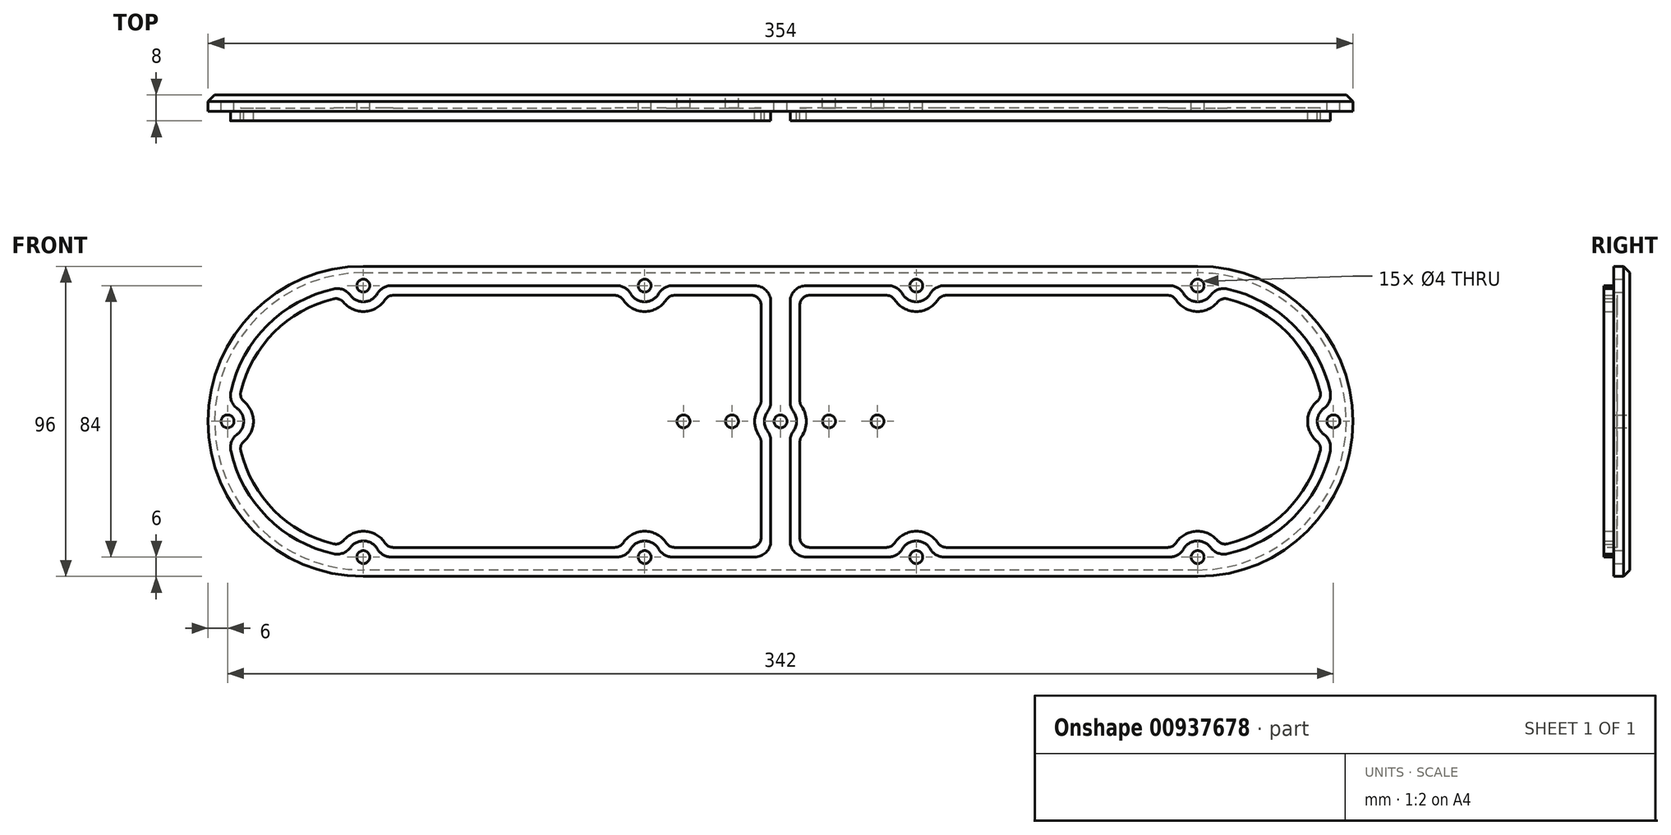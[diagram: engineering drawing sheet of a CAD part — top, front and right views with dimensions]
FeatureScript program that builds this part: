
annotation { "Feature Type Name" : "Feature", "Feature Type Description" : "" }
export const myFeature = defineFeature(function(context is Context, id is Id, definition is map)
    precondition{}
    {
        {
            var Q0;
            Q0=qCreatedBy(makeId("Front.planeOp"),FACE);
            var sketch = newSketch(context, id + "F0", { "sketchPlane" : qUnion([Q0])});
            skLineSegment(sketch, "E0", {"start": v(0, -113.77) * mm, "end": v(0, 113.17) * mm, "construction": true});
            skArc(sketch, "E1", {"start": v(129, 48) * mm, "mid": v(177, 0) * mm, "end": v(129, -48) * mm});
            skLineSegment(sketch, "E2", {"start": v(129, -48) * mm, "end": v(0, -48) * mm});
            skLineSegment(sketch, "E3", {"start": v(129, 48) * mm, "end": v(0, 48) * mm});
            skLineSegment(sketch, "E4.MirrorCS", {"start": v(-129, -48) * mm, "end": v(0, -48) * mm});
            skLineSegment(sketch, "E5.MirrorCS", {"start": v(-129, 48) * mm, "end": v(0, 48) * mm});
            skArc(sketch, "E6.MirrorCS", {"start": v(-129, 48) * mm, "mid": v(-177, 0) * mm, "end": v(-129, -48) * mm});
            skLineSegment(sketch, "E7", {"start": v(124, 42) * mm, "end": v(47, 42) * mm});
            skLineSegment(sketch, "E8", {"start": v(124, -42) * mm, "end": v(47, -42) * mm});
            skLineSegment(sketch, "E9", {"start": v(3, 42) * mm, "end": v(3, 4) * mm});
            skLineSegment(sketch, "E10.MirrorCS", {"start": v(-3, 42) * mm, "end": v(-3, 4) * mm});
            skCircle(sketch, "E11", {"center": v(42, 42) * mm, "radius": 2 * mm});
            skCircle(sketch, "E12.1.0", {"center": v(42, -42) * mm, "radius": 2 * mm});
            skCircle(sketch, "E13", {"center": v(0, 0) * mm, "radius": 2 * mm});
            skArc(sketch, "E14", {"start": v(170.7, 5) * mm, "mid": v(166, 0) * mm, "end": v(170.7, -5) * mm});
            skArc(sketch, "E15.trimOffspring", {"start": v(170.7, 5) * mm, "mid": v(158.7, 29.7) * mm, "end": v(134, 41.7) * mm});
            skArc(sketch, "E16", {"start": v(124, 42) * mm, "mid": v(128.85, 37) * mm, "end": v(134, 41.7) * mm});
            skArc(sketch, "E17", {"start": v(-3, 4) * mm, "mid": v(-5, 0) * mm, "end": v(-3, -4) * mm});
            skLineSegment(sketch, "E18.trimOffspring", {"start": v(-3, -4) * mm, "end": v(-3, -42) * mm});
            skLineSegment(sketch, "E19.trimOffspring", {"start": v(3, -4) * mm, "end": v(3, -42) * mm});
            skArc(sketch, "E20.trimOffspring", {"start": v(3, -4) * mm, "mid": v(5, 0) * mm, "end": v(3, 4) * mm});
            skArc(sketch, "E21", {"start": v(124, -42) * mm, "mid": v(128.85, -37) * mm, "end": v(134, -41.7) * mm});
            skArc(sketch, "E22.trimOffspring", {"start": v(134, -41.7) * mm, "mid": v(158.7, -29.7) * mm, "end": v(170.7, -5) * mm});
            skArc(sketch, "E23", {"start": v(37, 42) * mm, "mid": v(42, 37) * mm, "end": v(47, 42) * mm});
            skLineSegment(sketch, "E24.trimOffspring", {"start": v(37, 42) * mm, "end": v(3, 42) * mm});
            skArc(sketch, "E25", {"start": v(37, -42) * mm, "mid": v(42, -37) * mm, "end": v(47, -42) * mm});
            skLineSegment(sketch, "E26.trimOffspring", {"start": v(37, -42) * mm, "end": v(3, -42) * mm});
            skLineSegment(sketch, "E27.MirrorCS", {"start": v(-37, 42) * mm, "end": v(-3, 42) * mm});
            skLineSegment(sketch, "E28.MirrorCS", {"start": v(-124, 42) * mm, "end": v(-47, 42) * mm});
            skArc(sketch, "E29.MirrorCS", {"start": v(-37, 42) * mm, "mid": v(-42, 37) * mm, "end": v(-47, 42) * mm});
            skArc(sketch, "E30.MirrorCS", {"start": v(-124, 42) * mm, "mid": v(-128.85, 37) * mm, "end": v(-134, 41.7) * mm});
            skArc(sketch, "E31.MirrorCS", {"start": v(-170.7, 5) * mm, "mid": v(-158.7, 29.7) * mm, "end": v(-134, 41.7) * mm});
            skArc(sketch, "E32.MirrorCS", {"start": v(-170.7, 5) * mm, "mid": v(-166, 0) * mm, "end": v(-170.7, -5) * mm});
            skArc(sketch, "E33.MirrorCS", {"start": v(-134, -41.7) * mm, "mid": v(-158.7, -29.7) * mm, "end": v(-170.7, -5) * mm});
            skLineSegment(sketch, "E34.MirrorCS", {"start": v(-37, -42) * mm, "end": v(-3, -42) * mm});
            skArc(sketch, "E35.MirrorCS", {"start": v(-37, -42) * mm, "mid": v(-42, -37) * mm, "end": v(-47, -42) * mm});
            skLineSegment(sketch, "E36.MirrorCS", {"start": v(-124, -42) * mm, "end": v(-47, -42) * mm});
            skArc(sketch, "E37.MirrorCS", {"start": v(-124, -42) * mm, "mid": v(-128.85, -37) * mm, "end": v(-134, -41.7) * mm});
            skLineSegment(sketch, "E38", {"start": v(-28.33, 0) * mm, "end": v(22.4, 0) * mm, "construction": true});
            skCircle(sketch, "E39", {"center": v(129, 42) * mm, "radius": 2 * mm});
            skCircle(sketch, "E40.2.0", {"center": v(129, -42) * mm, "radius": 2 * mm});
            skCircle(sketch, "E40.3.0", {"center": v(171, 0) * mm, "radius": 2 * mm});
            skCircle(sketch, "E41.MirrorC", {"center": v(-42, 42) * mm, "radius": 2 * mm});
            skCircle(sketch, "E42.MirrorC", {"center": v(-129, 42) * mm, "radius": 2 * mm});
            skCircle(sketch, "E43.MirrorC", {"center": v(-171, 0) * mm, "radius": 2 * mm});
            skCircle(sketch, "E44.MirrorC", {"center": v(-129, -42) * mm, "radius": 2 * mm});
            skCircle(sketch, "E45.MirrorC", {"center": v(-42, -42) * mm, "radius": 2 * mm});
            skLineSegment(sketch, "E46.0", {"start": v(34.58, 39) * mm, "end": v(6, 39) * mm});
            skArc(sketch, "E46.1", {"start": v(34.58, 39) * mm, "mid": v(42, 34) * mm, "end": v(49.42, 39) * mm});
            skLineSegment(sketch, "E46.2", {"start": v(121.58, 39) * mm, "end": v(49.42, 39) * mm});
            skArc(sketch, "E46.3", {"start": v(34.58, -39) * mm, "mid": v(42, -34) * mm, "end": v(49.42, -39) * mm});
            skLineSegment(sketch, "E46.4", {"start": v(34.58, -39) * mm, "end": v(6, -39) * mm});
            skLineSegment(sketch, "E46.5", {"start": v(6, -5.3) * mm, "end": v(6, -39) * mm});
            skArc(sketch, "E46.6", {"start": v(6, -5.3) * mm, "mid": v(8, 0) * mm, "end": v(6, 5.3) * mm});
            skLineSegment(sketch, "E46.7", {"start": v(121.58, -39) * mm, "end": v(49.42, -39) * mm});
            skArc(sketch, "E46.8", {"start": v(121.58, -39) * mm, "mid": v(128.64, -34) * mm, "end": v(136.12, -38.35) * mm});
            skArc(sketch, "E46.9", {"start": v(136.12, -38.35) * mm, "mid": v(156.58, -27.58) * mm, "end": v(167.35, -7.12) * mm});
            skLineSegment(sketch, "E46.10", {"start": v(6, 39) * mm, "end": v(6, 5.3) * mm});
            skArc(sketch, "E46.11", {"start": v(167.35, 7.12) * mm, "mid": v(163, 0) * mm, "end": v(167.35, -7.12) * mm});
            skArc(sketch, "E46.12", {"start": v(167.35, 7.12) * mm, "mid": v(156.58, 27.58) * mm, "end": v(136.12, 38.35) * mm});
            skArc(sketch, "E46.13", {"start": v(121.58, 39) * mm, "mid": v(128.64, 34) * mm, "end": v(136.12, 38.35) * mm});
            skLineSegment(sketch, "E47.MirrorCS", {"start": v(-6, -5.3) * mm, "end": v(-6, -39) * mm});
            skArc(sketch, "E48.MirrorCS", {"start": v(-6, -5.3) * mm, "mid": v(-8, 0) * mm, "end": v(-6, 5.3) * mm});
            skLineSegment(sketch, "E49.MirrorCS", {"start": v(-6, 39) * mm, "end": v(-6, 5.3) * mm});
            skLineSegment(sketch, "E50.MirrorCS", {"start": v(-34.58, 39) * mm, "end": v(-6, 39) * mm});
            skLineSegment(sketch, "E51.MirrorCS", {"start": v(-121.58, 39) * mm, "end": v(-49.42, 39) * mm});
            skArc(sketch, "E52.MirrorCS", {"start": v(-34.58, 39) * mm, "mid": v(-42, 34) * mm, "end": v(-49.42, 39) * mm});
            skArc(sketch, "E53.MirrorCS", {"start": v(-121.58, 39) * mm, "mid": v(-128.64, 34) * mm, "end": v(-136.12, 38.35) * mm});
            skArc(sketch, "E54.MirrorCS", {"start": v(-167.35, 7.12) * mm, "mid": v(-156.58, 27.58) * mm, "end": v(-136.12, 38.35) * mm});
            skArc(sketch, "E55.MirrorCS", {"start": v(-167.35, 7.12) * mm, "mid": v(-163, 0) * mm, "end": v(-167.35, -7.12) * mm});
            skArc(sketch, "E56.MirrorCS", {"start": v(-136.12, -38.35) * mm, "mid": v(-156.58, -27.58) * mm, "end": v(-167.35, -7.12) * mm});
            skArc(sketch, "E57.MirrorCS", {"start": v(-121.58, -39) * mm, "mid": v(-128.64, -34) * mm, "end": v(-136.12, -38.35) * mm});
            skLineSegment(sketch, "E58.MirrorCS", {"start": v(-121.58, -39) * mm, "end": v(-49.42, -39) * mm});
            skArc(sketch, "E59.MirrorCS", {"start": v(-34.58, -39) * mm, "mid": v(-42, -34) * mm, "end": v(-49.42, -39) * mm});
            skLineSegment(sketch, "E60.MirrorCS", {"start": v(-34.58, -39) * mm, "end": v(-6, -39) * mm});
            skCircle(sketch, "E61", {"center": v(15, 0) * mm, "radius": 2 * mm});
            skCircle(sketch, "E62", {"center": v(30, 0) * mm, "radius": 2 * mm});
            skCircle(sketch, "E63.MirrorC", {"center": v(-15, 0) * mm, "radius": 2 * mm});
            skCircle(sketch, "E64.MirrorC", {"center": v(-30, 0) * mm, "radius": 2 * mm});
            skSolve(sketch);
        }
        {
            var Q0;
            Q0=qSketchRegion(id+"F0",true);
            extrude(context, id + "F1", {"entities" : qUnion([Q0]), "depth" : 5 * mm, "offsetDistance" : 25 * mm});
        }
        {
            var Q0;
            Q0=makeQuery(id+"F1.opExtrude","SWEPT_EDGE",EDGE,{"disambiguationData":[OSD([sQuery(id+"F0.wireOp",EDGE,"E9"),sQuery(id+"F0.wireOp",EDGE,"E24.trimOffspring")])]});
            var Q1;
            Q1=makeQuery(id+"F1.opExtrude","SWEPT_EDGE",EDGE,{"disambiguationData":[OSD([sQuery(id+"F0.wireOp",EDGE,"E19.trimOffspring"),sQuery(id+"F0.wireOp",EDGE,"E26.trimOffspring")])]});
            var Q2;
            Q2=makeQuery(id+"F1.opExtrude","SWEPT_EDGE",EDGE,{"disambiguationData":[OSD([sQuery(id+"F0.wireOp",EDGE,"E25"),sQuery(id+"F0.wireOp",EDGE,"E26.trimOffspring")])]});
            var Q3;
            Q3=makeQuery(id+"F1.opExtrude","SWEPT_EDGE",EDGE,{"disambiguationData":[OSD([sQuery(id+"F0.wireOp",EDGE,"E8"),sQuery(id+"F0.wireOp",EDGE,"E25")])]});
            var Q4;
            Q4=makeQuery(id+"F1.opExtrude","SWEPT_EDGE",EDGE,{"disambiguationData":[OSD([sQuery(id+"F0.wireOp",EDGE,"E8"),sQuery(id+"F0.wireOp",EDGE,"E21")])]});
            var Q5;
            Q5=makeQuery(id+"F1.opExtrude","SWEPT_EDGE",EDGE,{"disambiguationData":[OSD([sQuery(id+"F0.wireOp",EDGE,"E21"),sQuery(id+"F0.wireOp",EDGE,"E22.trimOffspring")])]});
            var Q6;
            Q6=makeQuery(id+"F1.opExtrude","SWEPT_EDGE",EDGE,{"disambiguationData":[OSD([sQuery(id+"F0.wireOp",EDGE,"E14"),sQuery(id+"F0.wireOp",EDGE,"E22.trimOffspring")])]});
            var Q7;
            Q7=makeQuery(id+"F1.opExtrude","SWEPT_EDGE",EDGE,{"disambiguationData":[OSD([sQuery(id+"F0.wireOp",EDGE,"E14"),sQuery(id+"F0.wireOp",EDGE,"E15.trimOffspring")])]});
            var Q8;
            Q8=makeQuery(id+"F1.opExtrude","SWEPT_EDGE",EDGE,{"disambiguationData":[OSD([sQuery(id+"F0.wireOp",EDGE,"E7"),sQuery(id+"F0.wireOp",EDGE,"E16")])]});
            var Q9;
            Q9=makeQuery(id+"F1.opExtrude","SWEPT_EDGE",EDGE,{"disambiguationData":[OSD([sQuery(id+"F0.wireOp",EDGE,"E15.trimOffspring"),sQuery(id+"F0.wireOp",EDGE,"E16")])]});
            var Q10;
            Q10=makeQuery(id+"F1.opExtrude","SWEPT_EDGE",EDGE,{"disambiguationData":[OSD([sQuery(id+"F0.wireOp",EDGE,"E7"),sQuery(id+"F0.wireOp",EDGE,"E23")])]});
            var Q11;
            Q11=makeQuery(id+"F1.opExtrude","SWEPT_EDGE",EDGE,{"disambiguationData":[OSD([sQuery(id+"F0.wireOp",EDGE,"E23"),sQuery(id+"F0.wireOp",EDGE,"E24.trimOffspring")])]});
            var Q12;
            Q12=makeQuery(id+"F1.opExtrude","SWEPT_EDGE",EDGE,{"disambiguationData":[OSD([sQuery(id+"F0.wireOp",EDGE,"E19.trimOffspring"),sQuery(id+"F0.wireOp",EDGE,"E20.trimOffspring")])]});
            var Q13;
            Q13=makeQuery(id+"F1.opExtrude","SWEPT_EDGE",EDGE,{"disambiguationData":[OSD([sQuery(id+"F0.wireOp",EDGE,"E9"),sQuery(id+"F0.wireOp",EDGE,"E20.trimOffspring")])]});
            var Q14;
            Q14=makeQuery(id+"F1.opExtrude","SWEPT_EDGE",EDGE,{"disambiguationData":[OSD([sQuery(id+"F0.wireOp",EDGE,"E10.MirrorCS"),sQuery(id+"F0.wireOp",EDGE,"E27.MirrorCS")])]});
            var Q15;
            Q15=makeQuery(id+"F1.opExtrude","SWEPT_EDGE",EDGE,{"disambiguationData":[OSD([sQuery(id+"F0.wireOp",EDGE,"E17"),sQuery(id+"F0.wireOp",EDGE,"E18.trimOffspring")])]});
            var Q16;
            Q16=makeQuery(id+"F1.opExtrude","SWEPT_EDGE",EDGE,{"disambiguationData":[OSD([sQuery(id+"F0.wireOp",EDGE,"E10.MirrorCS"),sQuery(id+"F0.wireOp",EDGE,"E17")])]});
            var Q17;
            Q17=makeQuery(id+"F1.opExtrude","SWEPT_EDGE",EDGE,{"disambiguationData":[OSD([sQuery(id+"F0.wireOp",EDGE,"E18.trimOffspring"),sQuery(id+"F0.wireOp",EDGE,"E34.MirrorCS")])]});
            var Q18;
            Q18=makeQuery(id+"F1.opExtrude","SWEPT_EDGE",EDGE,{"disambiguationData":[OSD([sQuery(id+"F0.wireOp",EDGE,"E35.MirrorCS"),sQuery(id+"F0.wireOp",EDGE,"E36.MirrorCS")])]});
            var Q19;
            Q19=makeQuery(id+"F1.opExtrude","SWEPT_EDGE",EDGE,{"disambiguationData":[OSD([sQuery(id+"F0.wireOp",EDGE,"E34.MirrorCS"),sQuery(id+"F0.wireOp",EDGE,"E35.MirrorCS")])]});
            var Q20;
            Q20=makeQuery(id+"F1.opExtrude","SWEPT_EDGE",EDGE,{"disambiguationData":[OSD([sQuery(id+"F0.wireOp",EDGE,"E36.MirrorCS"),sQuery(id+"F0.wireOp",EDGE,"E37.MirrorCS")])]});
            var Q21;
            Q21=makeQuery(id+"F1.opExtrude","SWEPT_EDGE",EDGE,{"disambiguationData":[OSD([sQuery(id+"F0.wireOp",EDGE,"E33.MirrorCS"),sQuery(id+"F0.wireOp",EDGE,"E37.MirrorCS")])]});
            var Q22;
            Q22=makeQuery(id+"F1.opExtrude","SWEPT_EDGE",EDGE,{"disambiguationData":[OSD([sQuery(id+"F0.wireOp",EDGE,"E31.MirrorCS"),sQuery(id+"F0.wireOp",EDGE,"E32.MirrorCS")])]});
            var Q23;
            Q23=makeQuery(id+"F1.opExtrude","SWEPT_EDGE",EDGE,{"disambiguationData":[OSD([sQuery(id+"F0.wireOp",EDGE,"E32.MirrorCS"),sQuery(id+"F0.wireOp",EDGE,"E33.MirrorCS")])]});
            var Q24;
            Q24=makeQuery(id+"F1.opExtrude","SWEPT_EDGE",EDGE,{"disambiguationData":[OSD([sQuery(id+"F0.wireOp",EDGE,"E28.MirrorCS"),sQuery(id+"F0.wireOp",EDGE,"E30.MirrorCS")])]});
            var Q25;
            Q25=makeQuery(id+"F1.opExtrude","SWEPT_EDGE",EDGE,{"disambiguationData":[OSD([sQuery(id+"F0.wireOp",EDGE,"E30.MirrorCS"),sQuery(id+"F0.wireOp",EDGE,"E31.MirrorCS")])]});
            var Q26;
            Q26=makeQuery(id+"F1.opExtrude","SWEPT_EDGE",EDGE,{"disambiguationData":[OSD([sQuery(id+"F0.wireOp",EDGE,"E28.MirrorCS"),sQuery(id+"F0.wireOp",EDGE,"E29.MirrorCS")])]});
            var Q27;
            Q27=makeQuery(id+"F1.opExtrude","SWEPT_EDGE",EDGE,{"disambiguationData":[OSD([sQuery(id+"F0.wireOp",EDGE,"E27.MirrorCS"),sQuery(id+"F0.wireOp",EDGE,"E29.MirrorCS")])]});
            fillet(context, id + "F2", {"entities" : qUnion([Q0, Q1, Q2, Q3, Q4, Q5, Q6, Q7, Q8, Q9, Q10, Q11, Q12, Q13, Q14, Q15, Q16, Q17, Q18, Q19, Q20, Q21, Q22, Q23, Q24, Q25, Q26, Q27]), "radius" : 5 * mm, "tangentPropagation" : true, "allowEdgeOverflow" : false});
        }
        {
            var Q0;
            Q0=makeQuery(id+"F0.imprint","IMPRINT",FACE,{"disambiguationData":[TD([[makeQuery(id+"F0.imprint","IMPRINT",EDGE,{"derivedFrom":sQuery(id+"F0.wireOp",EDGE,"E10.MirrorCS")}),-1.0]])]});
            var Q1;
            Q1=makeQuery(id+"F0.imprint","IMPRINT",FACE,{"disambiguationData":[TD([[makeQuery(id+"F0.imprint","IMPRINT",EDGE,{"derivedFrom":sQuery(id+"F0.wireOp",EDGE,"E7")}),1.0]])]});
            extrude(context, id + "F3", {"entities" : qUnion([Q0, Q1]), "operationType" : NewBodyOperationType.ADD, "depth" : 8 * mm, "offsetDistance" : 25 * mm});
        }
        {
            var Q0;
            Q0=makeQuery(id+"F0.imprint","IMPRINT",FACE,{"disambiguationData":[TD([[makeQuery(id+"F0.imprint","IMPRINT",EDGE,{"derivedFrom":sQuery(id+"F0.wireOp",EDGE,"E46.0")}),1.0]])]});
            var Q1;
            Q1=makeQuery(id+"F0.imprint","IMPRINT",FACE,{"disambiguationData":[TD([[makeQuery(id+"F0.imprint","IMPRINT",EDGE,{"derivedFrom":sQuery(id+"F0.wireOp",EDGE,"E47.MirrorCS")}),-1.0]])]});
            extrude(context, id + "F4", {"entities" : qUnion([Q0, Q1]), "operationType" : NewBodyOperationType.ADD, "depth" : 4 * mm, "offsetDistance" : 25 * mm});
        }
        {
            var Q0;
            Q0=makeQuery(id+"F3.opExtrude","SWEPT_EDGE",EDGE,{"disambiguationData":[OSD([sQuery(id+"F0.wireOp",EDGE,"E23"),sQuery(id+"F0.wireOp",EDGE,"E24.trimOffspring")])]});
            var Q1;
            Q1=makeQuery(id+"F3.opExtrude","SWEPT_EDGE",EDGE,{"disambiguationData":[OSD([sQuery(id+"F0.wireOp",EDGE,"E7"),sQuery(id+"F0.wireOp",EDGE,"E23")])]});
            var Q2;
            Q2=makeQuery(id+"F3.opExtrude","SWEPT_EDGE",EDGE,{"disambiguationData":[OSD([sQuery(id+"F0.wireOp",EDGE,"E7"),sQuery(id+"F0.wireOp",EDGE,"E16")])]});
            var Q3;
            Q3=makeQuery(id+"F3.opExtrude","SWEPT_EDGE",EDGE,{"disambiguationData":[OSD([sQuery(id+"F0.wireOp",EDGE,"E15.trimOffspring"),sQuery(id+"F0.wireOp",EDGE,"E16")])]});
            var Q4;
            Q4=makeQuery(id+"F3.opExtrude","SWEPT_EDGE",EDGE,{"disambiguationData":[OSD([sQuery(id+"F0.wireOp",EDGE,"E14"),sQuery(id+"F0.wireOp",EDGE,"E15.trimOffspring")])]});
            var Q5;
            Q5=makeQuery(id+"F3.opExtrude","SWEPT_EDGE",EDGE,{"disambiguationData":[OSD([sQuery(id+"F0.wireOp",EDGE,"E14"),sQuery(id+"F0.wireOp",EDGE,"E22.trimOffspring")])]});
            var Q6;
            Q6=makeQuery(id+"F3.opExtrude","SWEPT_EDGE",EDGE,{"disambiguationData":[OSD([sQuery(id+"F0.wireOp",EDGE,"E21"),sQuery(id+"F0.wireOp",EDGE,"E22.trimOffspring")])]});
            var Q7;
            Q7=makeQuery(id+"F3.opExtrude","SWEPT_EDGE",EDGE,{"disambiguationData":[OSD([sQuery(id+"F0.wireOp",EDGE,"E8"),sQuery(id+"F0.wireOp",EDGE,"E21")])]});
            var Q8;
            Q8=makeQuery(id+"F3.opExtrude","SWEPT_EDGE",EDGE,{"disambiguationData":[OSD([sQuery(id+"F0.wireOp",EDGE,"E8"),sQuery(id+"F0.wireOp",EDGE,"E25")])]});
            var Q9;
            Q9=makeQuery(id+"F3.opExtrude","SWEPT_EDGE",EDGE,{"disambiguationData":[OSD([sQuery(id+"F0.wireOp",EDGE,"E25"),sQuery(id+"F0.wireOp",EDGE,"E26.trimOffspring")])]});
            var Q10;
            Q10=makeQuery(id+"F3.opExtrude","SWEPT_EDGE",EDGE,{"disambiguationData":[OSD([sQuery(id+"F0.wireOp",EDGE,"E19.trimOffspring"),sQuery(id+"F0.wireOp",EDGE,"E26.trimOffspring")])]});
            var Q11;
            Q11=makeQuery(id+"F3.opExtrude","SWEPT_EDGE",EDGE,{"disambiguationData":[OSD([sQuery(id+"F0.wireOp",EDGE,"E19.trimOffspring"),sQuery(id+"F0.wireOp",EDGE,"E20.trimOffspring")])]});
            var Q12;
            Q12=makeQuery(id+"F3.opExtrude","SWEPT_EDGE",EDGE,{"disambiguationData":[OSD([sQuery(id+"F0.wireOp",EDGE,"E9"),sQuery(id+"F0.wireOp",EDGE,"E20.trimOffspring")])]});
            var Q13;
            Q13=makeQuery(id+"F3.opExtrude","SWEPT_EDGE",EDGE,{"disambiguationData":[OSD([sQuery(id+"F0.wireOp",EDGE,"E10.MirrorCS"),sQuery(id+"F0.wireOp",EDGE,"E17")])]});
            var Q14;
            Q14=makeQuery(id+"F3.opExtrude","SWEPT_EDGE",EDGE,{"disambiguationData":[OSD([sQuery(id+"F0.wireOp",EDGE,"E17"),sQuery(id+"F0.wireOp",EDGE,"E18.trimOffspring")])]});
            var Q15;
            Q15=makeQuery(id+"F3.opExtrude","SWEPT_EDGE",EDGE,{"disambiguationData":[OSD([sQuery(id+"F0.wireOp",EDGE,"E10.MirrorCS"),sQuery(id+"F0.wireOp",EDGE,"E27.MirrorCS")])]});
            var Q16;
            Q16=makeQuery(id+"F3.opExtrude","SWEPT_EDGE",EDGE,{"disambiguationData":[OSD([sQuery(id+"F0.wireOp",EDGE,"E9"),sQuery(id+"F0.wireOp",EDGE,"E24.trimOffspring")])]});
            var Q17;
            Q17=makeQuery(id+"F3.opExtrude","SWEPT_EDGE",EDGE,{"disambiguationData":[OSD([sQuery(id+"F0.wireOp",EDGE,"E27.MirrorCS"),sQuery(id+"F0.wireOp",EDGE,"E29.MirrorCS")])]});
            var Q18;
            Q18=makeQuery(id+"F3.opExtrude","SWEPT_EDGE",EDGE,{"disambiguationData":[OSD([sQuery(id+"F0.wireOp",EDGE,"E28.MirrorCS"),sQuery(id+"F0.wireOp",EDGE,"E29.MirrorCS")])]});
            var Q19;
            Q19=makeQuery(id+"F3.opExtrude","SWEPT_EDGE",EDGE,{"disambiguationData":[OSD([sQuery(id+"F0.wireOp",EDGE,"E28.MirrorCS"),sQuery(id+"F0.wireOp",EDGE,"E30.MirrorCS")])]});
            var Q20;
            Q20=makeQuery(id+"F3.opExtrude","SWEPT_EDGE",EDGE,{"disambiguationData":[OSD([sQuery(id+"F0.wireOp",EDGE,"E30.MirrorCS"),sQuery(id+"F0.wireOp",EDGE,"E31.MirrorCS")])]});
            var Q21;
            Q21=makeQuery(id+"F3.opExtrude","SWEPT_EDGE",EDGE,{"disambiguationData":[OSD([sQuery(id+"F0.wireOp",EDGE,"E31.MirrorCS"),sQuery(id+"F0.wireOp",EDGE,"E32.MirrorCS")])]});
            var Q22;
            Q22=makeQuery(id+"F3.opExtrude","SWEPT_EDGE",EDGE,{"disambiguationData":[OSD([sQuery(id+"F0.wireOp",EDGE,"E32.MirrorCS"),sQuery(id+"F0.wireOp",EDGE,"E33.MirrorCS")])]});
            var Q23;
            Q23=makeQuery(id+"F3.opExtrude","SWEPT_EDGE",EDGE,{"disambiguationData":[OSD([sQuery(id+"F0.wireOp",EDGE,"E36.MirrorCS"),sQuery(id+"F0.wireOp",EDGE,"E37.MirrorCS")])]});
            var Q24;
            Q24=makeQuery(id+"F3.opExtrude","SWEPT_EDGE",EDGE,{"disambiguationData":[OSD([sQuery(id+"F0.wireOp",EDGE,"E33.MirrorCS"),sQuery(id+"F0.wireOp",EDGE,"E37.MirrorCS")])]});
            var Q25;
            Q25=makeQuery(id+"F3.opExtrude","SWEPT_EDGE",EDGE,{"disambiguationData":[OSD([sQuery(id+"F0.wireOp",EDGE,"E35.MirrorCS"),sQuery(id+"F0.wireOp",EDGE,"E36.MirrorCS")])]});
            var Q26;
            Q26=makeQuery(id+"F3.opExtrude","SWEPT_EDGE",EDGE,{"disambiguationData":[OSD([sQuery(id+"F0.wireOp",EDGE,"E34.MirrorCS"),sQuery(id+"F0.wireOp",EDGE,"E35.MirrorCS")])]});
            var Q27;
            Q27=makeQuery(id+"F3.opExtrude","SWEPT_EDGE",EDGE,{"disambiguationData":[OSD([sQuery(id+"F0.wireOp",EDGE,"E18.trimOffspring"),sQuery(id+"F0.wireOp",EDGE,"E34.MirrorCS")])]});
            fillet(context, id + "F5", {"entities" : qUnion([Q0, Q1, Q2, Q3, Q4, Q5, Q6, Q7, Q8, Q9, Q10, Q11, Q12, Q13, Q14, Q15, Q16, Q17, Q18, Q19, Q20, Q21, Q22, Q23, Q24, Q25, Q26, Q27]), "radius" : 5 * mm, "tangentPropagation" : true, "allowEdgeOverflow" : false});
        }
        {
            var Q0;
            Q0=makeQuery(id+"F3.opExtrude","SWEPT_EDGE",EDGE,{"disambiguationData":[OSD([sQuery(id+"F0.wireOp",EDGE,"E46.6"),sQuery(id+"F0.wireOp",EDGE,"E46.10")])]});
            var Q1;
            Q1=makeQuery(id+"F3.opExtrude","SWEPT_EDGE",EDGE,{"disambiguationData":[OSD([sQuery(id+"F0.wireOp",EDGE,"E46.5"),sQuery(id+"F0.wireOp",EDGE,"E46.6")])]});
            var Q2;
            Q2=makeQuery(id+"F3.opExtrude","SWEPT_EDGE",EDGE,{"disambiguationData":[OSD([sQuery(id+"F0.wireOp",EDGE,"E47.MirrorCS"),sQuery(id+"F0.wireOp",EDGE,"E48.MirrorCS")])]});
            var Q3;
            Q3=makeQuery(id+"F3.opExtrude","SWEPT_EDGE",EDGE,{"disambiguationData":[OSD([sQuery(id+"F0.wireOp",EDGE,"E48.MirrorCS"),sQuery(id+"F0.wireOp",EDGE,"E49.MirrorCS")])]});
            var Q4;
            Q4=makeQuery(id+"F3.opExtrude","SWEPT_EDGE",EDGE,{"disambiguationData":[OSD([sQuery(id+"F0.wireOp",EDGE,"E49.MirrorCS"),sQuery(id+"F0.wireOp",EDGE,"E50.MirrorCS")])]});
            var Q5;
            Q5=makeQuery(id+"F3.opExtrude","SWEPT_EDGE",EDGE,{"disambiguationData":[OSD([sQuery(id+"F0.wireOp",EDGE,"E46.0"),sQuery(id+"F0.wireOp",EDGE,"E46.10")])]});
            var Q6;
            Q6=makeQuery(id+"F3.opExtrude","SWEPT_EDGE",EDGE,{"disambiguationData":[OSD([sQuery(id+"F0.wireOp",EDGE,"E50.MirrorCS"),sQuery(id+"F0.wireOp",EDGE,"E52.MirrorCS")])]});
            var Q7;
            Q7=makeQuery(id+"F3.opExtrude","SWEPT_EDGE",EDGE,{"disambiguationData":[OSD([sQuery(id+"F0.wireOp",EDGE,"E46.0"),sQuery(id+"F0.wireOp",EDGE,"E46.1")])]});
            var Q8;
            Q8=makeQuery(id+"F3.opExtrude","SWEPT_EDGE",EDGE,{"disambiguationData":[OSD([sQuery(id+"F0.wireOp",EDGE,"E51.MirrorCS"),sQuery(id+"F0.wireOp",EDGE,"E52.MirrorCS")])]});
            var Q9;
            Q9=makeQuery(id+"F3.opExtrude","SWEPT_EDGE",EDGE,{"disambiguationData":[OSD([sQuery(id+"F0.wireOp",EDGE,"E53.MirrorCS"),sQuery(id+"F0.wireOp",EDGE,"E54.MirrorCS")])]});
            var Q10;
            Q10=makeQuery(id+"F3.opExtrude","SWEPT_EDGE",EDGE,{"disambiguationData":[OSD([sQuery(id+"F0.wireOp",EDGE,"E51.MirrorCS"),sQuery(id+"F0.wireOp",EDGE,"E53.MirrorCS")])]});
            var Q11;
            Q11=makeQuery(id+"F3.opExtrude","SWEPT_EDGE",EDGE,{"disambiguationData":[OSD([sQuery(id+"F0.wireOp",EDGE,"E55.MirrorCS"),sQuery(id+"F0.wireOp",EDGE,"E56.MirrorCS")])]});
            var Q12;
            Q12=makeQuery(id+"F3.opExtrude","SWEPT_EDGE",EDGE,{"disambiguationData":[OSD([sQuery(id+"F0.wireOp",EDGE,"E54.MirrorCS"),sQuery(id+"F0.wireOp",EDGE,"E55.MirrorCS")])]});
            var Q13;
            Q13=makeQuery(id+"F3.opExtrude","SWEPT_EDGE",EDGE,{"disambiguationData":[OSD([sQuery(id+"F0.wireOp",EDGE,"E57.MirrorCS"),sQuery(id+"F0.wireOp",EDGE,"E58.MirrorCS")])]});
            var Q14;
            Q14=makeQuery(id+"F3.opExtrude","SWEPT_EDGE",EDGE,{"disambiguationData":[OSD([sQuery(id+"F0.wireOp",EDGE,"E56.MirrorCS"),sQuery(id+"F0.wireOp",EDGE,"E57.MirrorCS")])]});
            var Q15;
            Q15=makeQuery(id+"F3.opExtrude","SWEPT_EDGE",EDGE,{"disambiguationData":[OSD([sQuery(id+"F0.wireOp",EDGE,"E47.MirrorCS"),sQuery(id+"F0.wireOp",EDGE,"E60.MirrorCS")])]});
            var Q16;
            Q16=makeQuery(id+"F3.opExtrude","SWEPT_EDGE",EDGE,{"disambiguationData":[OSD([sQuery(id+"F0.wireOp",EDGE,"E58.MirrorCS"),sQuery(id+"F0.wireOp",EDGE,"E59.MirrorCS")])]});
            var Q17;
            Q17=makeQuery(id+"F3.opExtrude","SWEPT_EDGE",EDGE,{"disambiguationData":[OSD([sQuery(id+"F0.wireOp",EDGE,"E59.MirrorCS"),sQuery(id+"F0.wireOp",EDGE,"E60.MirrorCS")])]});
            var Q18;
            Q18=makeQuery(id+"F3.opExtrude","SWEPT_EDGE",EDGE,{"disambiguationData":[OSD([sQuery(id+"F0.wireOp",EDGE,"E46.4"),sQuery(id+"F0.wireOp",EDGE,"E46.5")])]});
            var Q19;
            Q19=makeQuery(id+"F3.opExtrude","SWEPT_EDGE",EDGE,{"disambiguationData":[OSD([sQuery(id+"F0.wireOp",EDGE,"E46.3"),sQuery(id+"F0.wireOp",EDGE,"E46.7")])]});
            var Q20;
            Q20=makeQuery(id+"F3.opExtrude","SWEPT_EDGE",EDGE,{"disambiguationData":[OSD([sQuery(id+"F0.wireOp",EDGE,"E46.3"),sQuery(id+"F0.wireOp",EDGE,"E46.4")])]});
            var Q21;
            Q21=makeQuery(id+"F3.opExtrude","SWEPT_EDGE",EDGE,{"disambiguationData":[OSD([sQuery(id+"F0.wireOp",EDGE,"E46.7"),sQuery(id+"F0.wireOp",EDGE,"E46.8")])]});
            var Q22;
            Q22=makeQuery(id+"F3.opExtrude","SWEPT_EDGE",EDGE,{"disambiguationData":[OSD([sQuery(id+"F0.wireOp",EDGE,"E46.8"),sQuery(id+"F0.wireOp",EDGE,"E46.9")])]});
            var Q23;
            Q23=makeQuery(id+"F3.opExtrude","SWEPT_EDGE",EDGE,{"disambiguationData":[OSD([sQuery(id+"F0.wireOp",EDGE,"E46.9"),sQuery(id+"F0.wireOp",EDGE,"E46.11")])]});
            var Q24;
            Q24=makeQuery(id+"F3.opExtrude","SWEPT_EDGE",EDGE,{"disambiguationData":[OSD([sQuery(id+"F0.wireOp",EDGE,"E46.11"),sQuery(id+"F0.wireOp",EDGE,"E46.12")])]});
            var Q25;
            Q25=makeQuery(id+"F3.opExtrude","SWEPT_EDGE",EDGE,{"disambiguationData":[OSD([sQuery(id+"F0.wireOp",EDGE,"E46.2"),sQuery(id+"F0.wireOp",EDGE,"E46.13")])]});
            var Q26;
            Q26=makeQuery(id+"F3.opExtrude","SWEPT_EDGE",EDGE,{"disambiguationData":[OSD([sQuery(id+"F0.wireOp",EDGE,"E46.12"),sQuery(id+"F0.wireOp",EDGE,"E46.13")])]});
            var Q27;
            Q27=makeQuery(id+"F3.opExtrude","SWEPT_EDGE",EDGE,{"disambiguationData":[OSD([sQuery(id+"F0.wireOp",EDGE,"E46.1"),sQuery(id+"F0.wireOp",EDGE,"E46.2")])]});
            fillet(context, id + "F6", {"entities" : qUnion([Q0, Q1, Q2, Q3, Q4, Q5, Q6, Q7, Q8, Q9, Q10, Q11, Q12, Q13, Q14, Q15, Q16, Q17, Q18, Q19, Q20, Q21, Q22, Q23, Q24, Q25, Q26, Q27]), "radius" : 3 * mm, "tangentPropagation" : true, "allowEdgeOverflow" : false});
        }
        {
            var Q0;
            Q0=makeQuery(id+"F1.opExtrude","CAP_EDGE",EDGE,{"disambiguationData":[OSD([sQuery(id+"F0.wireOp",EDGE,"E2"),sQuery(id+"F0.wireOp",EDGE,"E4.MirrorCS")])],"isStart":true});
            chamfer(context, id + "F7", {"entities" : qUnion([Q0]), "width" : 2 * mm, "tangentPropagation" : true});
        }
    });
